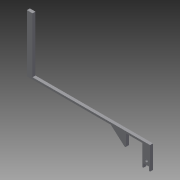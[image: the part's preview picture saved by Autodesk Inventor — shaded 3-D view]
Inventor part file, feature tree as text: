
AUTODESK INVENTOR PART (.ipt)
format: ipt  version: 2013 (Build 170138000, 138)  size: 99,840 bytes
history: native  units: in
note: dims shown in document units (in); Inventor stores cm internally (conversion verified against a paired STEP export)
features: extrude x1, sketch x1
ambient origin geometry x8: Origin, YZ Plane, XZ Plane, XY Plane, X Axis, Y Axis, Z Axis, Center Point
bodies: Solid1 (feature_tree)
feature tree (2):
  extrude  "Extrusion1"  Depth=0.5in
  sketch  "Sketch1"  dims[d0=0.125in d1=0.5in d2=0.75in d3=0.125in d4=0.5in d6=0.3765in d7=0.5in d8=3.0in d9=16.125in d10=0.25in d11=15.125in d13=2.0in d14=2.15in d15=1.0607in d16=0.75in d17=1.75in d18=0.125in d19=0.3875in d20=0.0in d21=7.5in d22=0.725in d24=0.375in d25=7.25in]
